# Revit family: Food-Service-Equipment_Oscartek_Italia_1-Pro-1500
name_source: partatom
category: Specialty Equipment
units: mm (PartAtom-declared; Revit-internal decimal feet)

## family parameters
Always vertical = Yes
Classification Number = 23.40.40.11.17
Cut with Voids When Loaded = No
Enable Cutting in Views = No
Maintain Annotation Orientation = No
Part Type = Normal
Room Calculation Point = No
Round Connector Dimension = Use Diameter
Shared = No
Work Plane-Based = No

## types (1)
- Food-Service-Equipment_Oscartek_Italia_1-Pro-1500
    Apparent Power = 972 VA
    BTUH = 3500.0 Btu/h
    Body Finish = QF_Metal-Stainless-Polished
    Building Codes = https://www.arcat.com
    CSI Master Format = Refrigerated Food Storage Cases
    CSI MasterFormat = 11 41 13
    Conn Conduit = Yes
    Construction Details = http://www.oscartek.com
    Cycle = 60 Hz
    Default Elevation = 0"
    Depth = 32 5/8"
    Description = ITALIA 1 PRO HIGH HUMIDITY COLD 1500
    FL Amps = 8 A
    Glass Frame Finish = QF_Plastic-Black-Smooth
    Green Building-LEED = https://www.arcat.com
    Indirect Waste Connection Height = 0"
    Indirect Waste Flow = 0 GPM
    Indirect Waste Size = 0"
    Installation-Fabrication = http://www.oscartek.com
    Manufacturer = OSCARTEK
    Manufacturer Fax = 650-342-7400
    Manufacturer Website = http://www.oscartek.com
    Max Overcurrent Protection = 0 A
    Min Ckt Ampacity = 0 A
    Model = ITALIA 1 PRO 1500
    Phase = 1
    Product Data = http://www.oscartek.com
    Refrigerant Type = R404A
    Refrigerant Volume = 0.00 kip
    Revision = R1_2018-10
    Sales Information = http://www.oscartek.com
    Specification = https://www.arcat.com
    Test Data = http://www.oscartek.com
    Type Comments = As Specified
    URL = www.oscartek.com
    URL Cutsheet = www.oscartek.com
    Volts = 120 V
    Watts = 900 W
    Weight in Pounds = 352
    Width = 59 3/16"

## geometry (parser evidence)
native form markers: Blend x44, Sweep x2
no freeform markers — native parametric forms only
